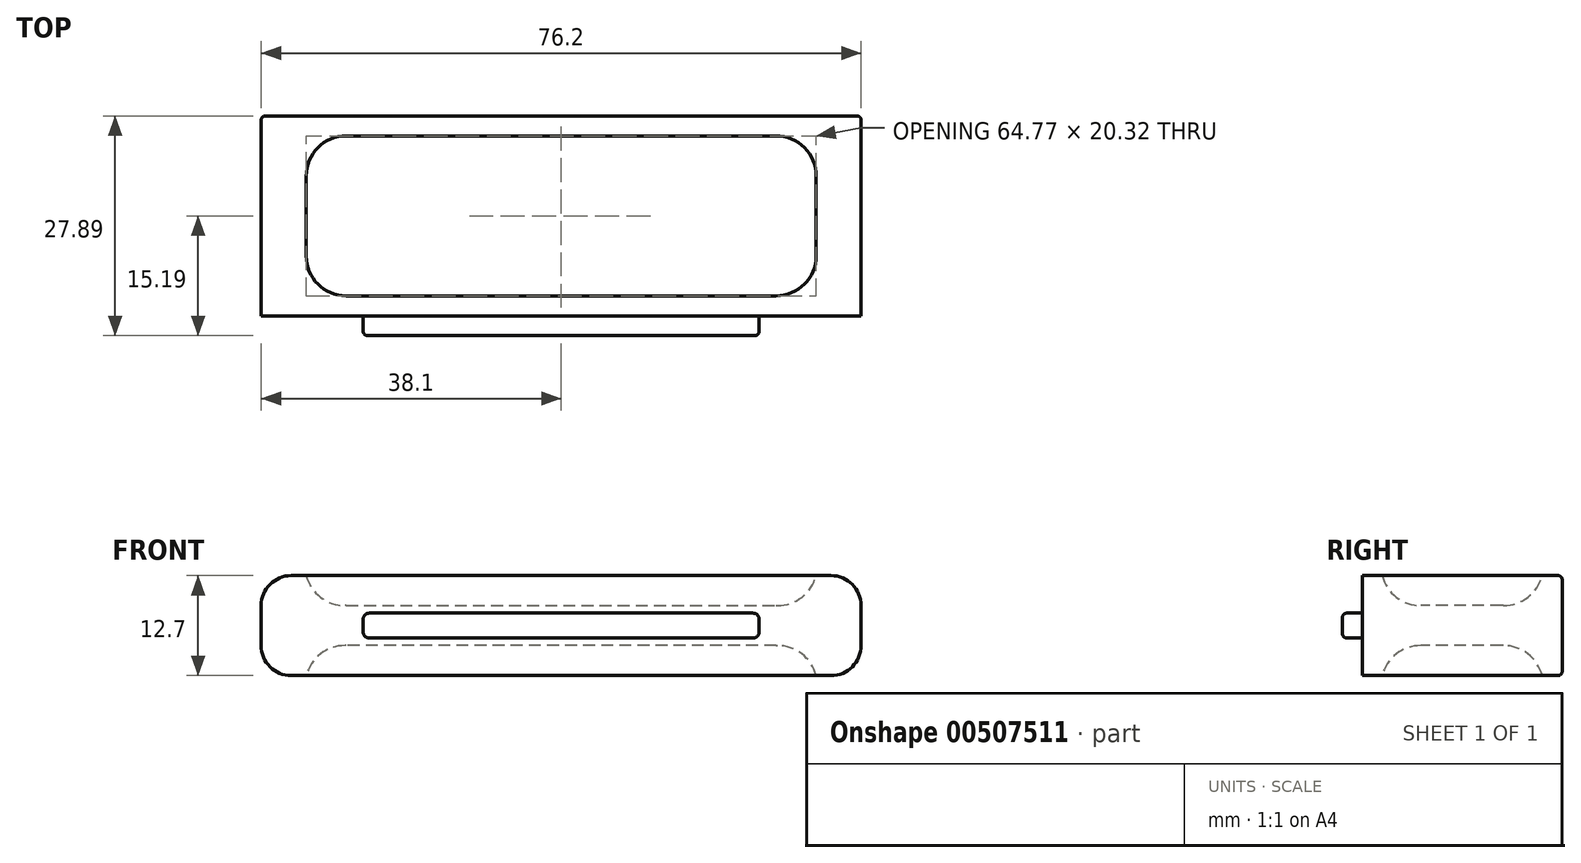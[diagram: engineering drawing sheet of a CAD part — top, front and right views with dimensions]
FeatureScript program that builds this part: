
annotation { "Feature Type Name" : "Feature", "Feature Type Description" : "" }
export const myFeature = defineFeature(function(context is Context, id is Id, definition is map)
    precondition{}
    {
        {
            var Q0;
            Q0=qCreatedBy(makeId("Front.planeOp"),FACE);
            var sketch = newSketch(context, id + "F0", { "sketchPlane" : qUnion([Q0])});
            skLineSegment(sketch, "E0.bottom", {"start": v(-38.1, 6.35) * mm, "end": v(38.1, 6.35) * mm});
            skLineSegment(sketch, "E0.top", {"start": v(-38.1, -6.35) * mm, "end": v(38.1, -6.35) * mm});
            skLineSegment(sketch, "E0.left", {"start": v(-38.1, 6.35) * mm, "end": v(-38.1, -6.35) * mm});
            skLineSegment(sketch, "E0.right", {"start": v(38.1, 6.35) * mm, "end": v(38.1, -6.35) * mm});
            skSolve(sketch);
        }
        {
            var Q0;
            Q0=makeQuery(id+"F0.imprint","IMPRINT",FACE,{"disambiguationData":[TD([[makeQuery(id+"F0.imprint","IMPRINT",EDGE,{"derivedFrom":sQuery(id+"F0.wireOp",EDGE,"E0.bottom")}),-1.0]])]});
            extrude(context, id + "F1", {"entities" : qUnion([Q0]), "depth" : 25.4 * mm, "offsetDistance" : 25.4 * mm});
        }
        {
            var Q0;
            Q0=makeQuery(id+"F1.opExtrude","CAP_FACE",FACE,{"disambiguationData":[OSD([sQuery(id+"F0.wireOp",EDGE,"E0.bottom"),sQuery(id+"F0.wireOp",EDGE,"E0.top"),sQuery(id+"F0.wireOp",EDGE,"E0.left"),sQuery(id+"F0.wireOp",EDGE,"E0.right")])],"isStart":false});
            var sketch = newSketch(context, id + "F2", { "sketchPlane" : qUnion([Q0])});
            skLineSegment(sketch, "E1.bottom", {"start": v(-25.15, 1.57) * mm, "end": v(25.15, 1.57) * mm});
            skLineSegment(sketch, "E1.top", {"start": v(-25.15, -1.57) * mm, "end": v(25.15, -1.57) * mm});
            skLineSegment(sketch, "E1.left", {"start": v(-25.15, 1.57) * mm, "end": v(-25.15, -1.57) * mm});
            skLineSegment(sketch, "E1.right", {"start": v(25.15, 1.57) * mm, "end": v(25.15, -1.57) * mm});
            skSolve(sketch);
        }
        {
            var Q0;
            Q0 = qSketchRegion(id + "F2", true);
            extrude(context, id + "F3", {"entities" : qUnion([Q0]), "operationType" : NewBodyOperationType.ADD, "depth" : 2.5 * mm, "offsetDistance" : 25.4 * mm});
        }
        {
            var Q0;
            Q0=makeQuery(id+"F3.opExtrude","SWEPT_EDGE",EDGE,{"disambiguationData":[OSD([sQuery(id+"F2.wireOp",EDGE,"E1.bottom"),sQuery(id+"F2.wireOp",EDGE,"E1.left")])]});
            var Q1;
            Q1=makeQuery(id+"F3.opExtrude","SWEPT_EDGE",EDGE,{"disambiguationData":[OSD([sQuery(id+"F2.wireOp",EDGE,"E1.top"),sQuery(id+"F2.wireOp",EDGE,"E1.left")])]});
            var Q2;
            Q2=makeQuery(id+"F3.opExtrude","SWEPT_EDGE",EDGE,{"disambiguationData":[OSD([sQuery(id+"F2.wireOp",EDGE,"E1.bottom"),sQuery(id+"F2.wireOp",EDGE,"E1.right")])]});
            var Q3;
            Q3=makeQuery(id+"F3.opExtrude","SWEPT_EDGE",EDGE,{"disambiguationData":[OSD([sQuery(id+"F2.wireOp",EDGE,"E1.top"),sQuery(id+"F2.wireOp",EDGE,"E1.right")])]});
            fillet(context, id + "F4", {"entities" : qUnion([Q0, Q1, Q2, Q3]), "radius" : 0.76 * mm, "tangentPropagation" : true, "allowEdgeOverflow" : false});
        }
        {
            var Q0;
            Q0=makeQuery(id+"F3.opExtrude","CAP_FACE",FACE,{"disambiguationData":[OSD([sQuery(id+"F2.wireOp",EDGE,"E1.bottom"),sQuery(id+"F2.wireOp",EDGE,"E1.top"),sQuery(id+"F2.wireOp",EDGE,"E1.left"),sQuery(id+"F2.wireOp",EDGE,"E1.right")])],"isStart":false});
            fillet(context, id + "F5", {"entities" : qUnion([Q0]), "radius" : 0.5 * mm, "tangentPropagation" : true, "allowEdgeOverflow" : false});
        }
        {
            var Q0;
            Q0=makeQuery(id+"F1.opExtrude","SWEPT_EDGE",EDGE,{"disambiguationData":[OSD([sQuery(id+"F0.wireOp",EDGE,"E0.bottom"),sQuery(id+"F0.wireOp",EDGE,"E0.right")])]});
            var Q1;
            Q1=makeQuery(id+"F1.opExtrude","SWEPT_EDGE",EDGE,{"disambiguationData":[OSD([sQuery(id+"F0.wireOp",EDGE,"E0.top"),sQuery(id+"F0.wireOp",EDGE,"E0.right")])]});
            var Q2;
            Q2=makeQuery(id+"F1.opExtrude","SWEPT_EDGE",EDGE,{"disambiguationData":[OSD([sQuery(id+"F0.wireOp",EDGE,"E0.bottom"),sQuery(id+"F0.wireOp",EDGE,"E0.left")])]});
            var Q3;
            Q3=makeQuery(id+"F1.opExtrude","SWEPT_EDGE",EDGE,{"disambiguationData":[OSD([sQuery(id+"F0.wireOp",EDGE,"E0.top"),sQuery(id+"F0.wireOp",EDGE,"E0.left")])]});
            fillet(context, id + "F6", {"entities" : qUnion([Q0, Q1, Q2, Q3]), "radius" : 3.8 * mm, "tangentPropagation" : true, "allowEdgeOverflow" : false});
        }
        {
            var Q0;
            Q0=makeQuery(id+"F1.opExtrude","SWEPT_FACE",FACE,{"disambiguationData":[OSD([sQuery(id+"F0.wireOp",EDGE,"E0.bottom")])]});
            var sketch = newSketch(context, id + "F7", { "sketchPlane" : qUnion([Q0])});
            skLineSegment(sketch, "E2.bottom", {"start": v(-32.39, -2.54) * mm, "end": v(32.39, -2.54) * mm});
            skLineSegment(sketch, "E2.top", {"start": v(-32.39, -22.86) * mm, "end": v(32.39, -22.86) * mm});
            skLineSegment(sketch, "E2.left", {"start": v(-32.39, -2.54) * mm, "end": v(-32.39, -22.86) * mm});
            skLineSegment(sketch, "E2.right", {"start": v(32.39, -2.54) * mm, "end": v(32.39, -22.86) * mm});
            skSolve(sketch);
        }
        {
            var Q0;
            Q0 = qSketchRegion(id + "F7", true);
            extrude(context, id + "F8", {"entities" : qUnion([Q0]), "operationType" : NewBodyOperationType.REMOVE, "oppositeDirection" : true, "depth" : 3.8 * mm, "offsetDistance" : 25.4 * mm});
        }
        {
            var Q0;
            Q0=makeQuery(id+"F8.boolean.opBoolean","COPY",EDGE,{"derivedFrom":makeQuery(id+"F8.opExtrude","SWEPT_EDGE",EDGE,{"disambiguationData":[OSD([sQuery(id+"F7.wireOp",EDGE,"E2.bottom"),sQuery(id+"F7.wireOp",EDGE,"E2.left")])]})});
            var Q1;
            Q1=makeQuery(id+"F8.boolean.opBoolean","COPY",EDGE,{"derivedFrom":makeQuery(id+"F8.opExtrude","SWEPT_EDGE",EDGE,{"disambiguationData":[OSD([sQuery(id+"F7.wireOp",EDGE,"E2.top"),sQuery(id+"F7.wireOp",EDGE,"E2.left")])]})});
            var Q2;
            Q2=makeQuery(id+"F8.boolean.opBoolean","COPY",EDGE,{"derivedFrom":makeQuery(id+"F8.opExtrude","SWEPT_EDGE",EDGE,{"disambiguationData":[OSD([sQuery(id+"F7.wireOp",EDGE,"E2.bottom"),sQuery(id+"F7.wireOp",EDGE,"E2.right")])]})});
            var Q3;
            Q3=makeQuery(id+"F8.boolean.opBoolean","COPY",EDGE,{"derivedFrom":makeQuery(id+"F8.opExtrude","SWEPT_EDGE",EDGE,{"disambiguationData":[OSD([sQuery(id+"F7.wireOp",EDGE,"E2.top"),sQuery(id+"F7.wireOp",EDGE,"E2.right")])]})});
            fillet(context, id + "F9", {"entities" : qUnion([Q0, Q1, Q2, Q3]), "radius" : 5.08 * mm, "tangentPropagation" : true, "allowEdgeOverflow" : false});
        }
        {
            var Q0;
            Q0=makeQuery(id+"F8.boolean.opBoolean","COPY",EDGE,{"derivedFrom":makeQuery(id+"F8.opExtrude","CAP_EDGE",EDGE,{"disambiguationData":[OSD([sQuery(id+"F7.wireOp",EDGE,"E2.bottom")])],"isStart":false})});
            fillet(context, id + "F10", {"entities" : qUnion([Q0]), "radius" : 5.08 * mm, "tangentPropagation" : true, "allowEdgeOverflow" : false});
        }
        {
            var Q0;
            Q0=makeQuery(id+"F1.opExtrude","SWEPT_FACE",FACE,{"disambiguationData":[OSD([sQuery(id+"F0.wireOp",EDGE,"E0.top")])]});
            var sketch = newSketch(context, id + "F11", { "sketchPlane" : qUnion([Q0])});
            skLineSegment(sketch, "E3.bottom", {"start": v(-32.39, 22.86) * mm, "end": v(32.39, 22.86) * mm});
            skLineSegment(sketch, "E3.top", {"start": v(-32.39, 2.54) * mm, "end": v(32.39, 2.54) * mm});
            skLineSegment(sketch, "E3.left", {"start": v(-32.39, 22.86) * mm, "end": v(-32.39, 2.54) * mm});
            skLineSegment(sketch, "E3.right", {"start": v(32.39, 22.86) * mm, "end": v(32.39, 2.54) * mm});
            skSolve(sketch);
        }
        {
            var Q0;
            Q0 = qSketchRegion(id + "F11", true);
            extrude(context, id + "F12", {"entities" : qUnion([Q0]), "operationType" : NewBodyOperationType.REMOVE, "oppositeDirection" : true, "depth" : 3.8 * mm, "offsetDistance" : 25.4 * mm});
        }
        {
            var Q0;
            Q0=makeQuery(id+"F12.boolean.opBoolean","COPY",EDGE,{"derivedFrom":makeQuery(id+"F12.opExtrude","SWEPT_EDGE",EDGE,{"disambiguationData":[OSD([sQuery(id+"F11.wireOp",EDGE,"E3.bottom"),sQuery(id+"F11.wireOp",EDGE,"E3.right")])]})});
            var Q1;
            Q1=makeQuery(id+"F12.boolean.opBoolean","COPY",EDGE,{"derivedFrom":makeQuery(id+"F12.opExtrude","SWEPT_EDGE",EDGE,{"disambiguationData":[OSD([sQuery(id+"F11.wireOp",EDGE,"E3.top"),sQuery(id+"F11.wireOp",EDGE,"E3.right")])]})});
            var Q2;
            Q2=makeQuery(id+"F12.boolean.opBoolean","COPY",EDGE,{"derivedFrom":makeQuery(id+"F12.opExtrude","SWEPT_EDGE",EDGE,{"disambiguationData":[OSD([sQuery(id+"F11.wireOp",EDGE,"E3.bottom"),sQuery(id+"F11.wireOp",EDGE,"E3.left")])]})});
            var Q3;
            Q3=makeQuery(id+"F12.boolean.opBoolean","COPY",EDGE,{"derivedFrom":makeQuery(id+"F12.opExtrude","SWEPT_EDGE",EDGE,{"disambiguationData":[OSD([sQuery(id+"F11.wireOp",EDGE,"E3.top"),sQuery(id+"F11.wireOp",EDGE,"E3.left")])]})});
            fillet(context, id + "F13", {"entities" : qUnion([Q0, Q1, Q2, Q3]), "radius" : 5.08 * mm, "tangentPropagation" : true, "allowEdgeOverflow" : false});
        }
        {
            var Q0;
            {var subQ0=sQuery(id+"F11.wireOp",EDGE,"E3.right");var subQ1=sQuery(id+"F11.wireOp",EDGE,"E3.bottom");Q0=makeQuery(id+"F13.opFillet","BLEND_EDGE",EDGE,{"blendedFrom":[makeQuery(id+"F12.boolean.opBoolean","COPY",EDGE,{"derivedFrom":makeQuery(id+"F12.opExtrude","SWEPT_EDGE",EDGE,{"disambiguationData":[OSD([subQ1,subQ0])]})}),makeQuery(id+"F12.boolean.opBoolean","COPY",FACE,{"derivedFrom":makeQuery(id+"F12.opExtrude","CAP_FACE",FACE,{"disambiguationData":[OSD([subQ1,sQuery(id+"F11.wireOp",EDGE,"E3.top"),sQuery(id+"F11.wireOp",EDGE,"E3.left"),subQ0])],"isStart":false})})],"blendedInto":[makeQuery(id+"F12.boolean.opBoolean","COPY",FACE,{"derivedFrom":makeQuery(id+"F12.opExtrude","CAP_FACE",FACE,{"disambiguationData":[OSD([subQ1,sQuery(id+"F11.wireOp",EDGE,"E3.top"),sQuery(id+"F11.wireOp",EDGE,"E3.left"),subQ0])],"isStart":false})})]});}
            fillet(context, id + "F14", {"entities" : qUnion([Q0]), "radius" : 5.08 * mm, "tangentPropagation" : true, "allowEdgeOverflow" : false});
        }
        {
            var Q0;
            {var subQ0=sQuery(id+"F0.wireOp",EDGE,"E0.left");var subQ1=sQuery(id+"F0.wireOp",EDGE,"E0.bottom");Q0=makeQuery(id+"F6.opFillet","BLEND_EDGE",EDGE,{"blendedFrom":[makeQuery(id+"F1.opExtrude","SWEPT_EDGE",EDGE,{"disambiguationData":[OSD([subQ1,subQ0])]}),makeQuery(id+"F1.opExtrude","CAP_FACE",FACE,{"disambiguationData":[OSD([subQ1,sQuery(id+"F0.wireOp",EDGE,"E0.top"),subQ0,sQuery(id+"F0.wireOp",EDGE,"E0.right")])],"isStart":true})],"blendedInto":[makeQuery(id+"F1.opExtrude","CAP_FACE",FACE,{"disambiguationData":[OSD([subQ1,sQuery(id+"F0.wireOp",EDGE,"E0.top"),subQ0,sQuery(id+"F0.wireOp",EDGE,"E0.right")])],"isStart":true})]});}
            fillet(context, id + "F15", {"entities" : qUnion([Q0]), "radius" : 0.5 * mm, "tangentPropagation" : true, "allowEdgeOverflow" : false});
        }
    });
